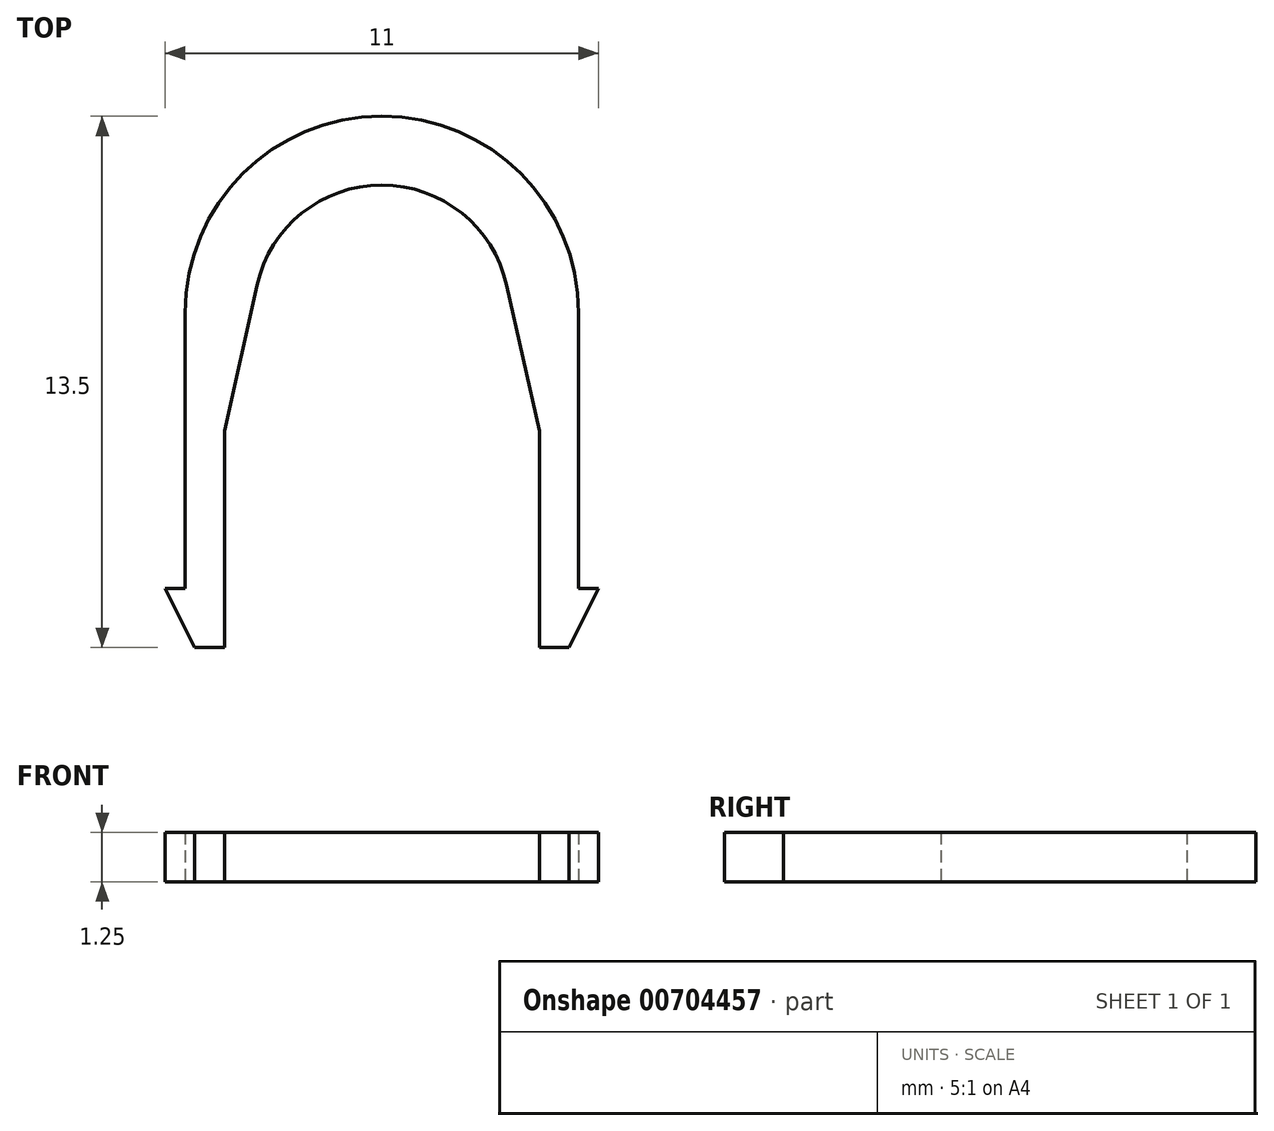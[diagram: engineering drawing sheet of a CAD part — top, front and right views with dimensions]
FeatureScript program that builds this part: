
annotation { "Feature Type Name" : "Feature", "Feature Type Description" : "" }
export const myFeature = defineFeature(function(context is Context, id is Id, definition is map)
    precondition{}
    {
        {
            var Q0;
            Q0=qCreatedBy(makeId("Top.planeOp"),FACE);
            var sketch = newSketch(context, id + "F0", { "sketchPlane" : qUnion([Q0])});
            skLineSegment(sketch, "E0", {"start": v(0, 0) * mm, "end": v(0, 5) * mm, "construction": true});
            skArc(sketch, "E1", {"start": v(5, 5) * mm, "mid": v(0, 10) * mm, "end": v(-5, 5) * mm});
            skLineSegment(sketch, "E2", {"start": v(-5, 5) * mm, "end": v(-5, -2) * mm});
            skLineSegment(sketch, "E3", {"start": v(-4, 2) * mm, "end": v(-4, -3.5) * mm});
            skLineSegment(sketch, "E4", {"start": v(-5, -2) * mm, "end": v(-5.5, -2) * mm});
            skLineSegment(sketch, "E5", {"start": v(-5.5, -2) * mm, "end": v(-4.75, -3.5) * mm});
            skLineSegment(sketch, "E6", {"start": v(-4, -3.5) * mm, "end": v(-4.75, -3.5) * mm});
            skLineSegment(sketch, "E7.MirrorCS", {"start": v(5, 5) * mm, "end": v(5, -2) * mm});
            skLineSegment(sketch, "E8.MirrorCS", {"start": v(5, -2) * mm, "end": v(5.5, -2) * mm});
            skLineSegment(sketch, "E9.MirrorCS", {"start": v(5.5, -2) * mm, "end": v(4.75, -3.5) * mm});
            skLineSegment(sketch, "E10.MirrorCS", {"start": v(4, -3.5) * mm, "end": v(4.75, -3.5) * mm});
            skLineSegment(sketch, "E11.MirrorCS", {"start": v(4, 2) * mm, "end": v(4, -3.5) * mm});
            skArc(sketch, "E12", {"start": v(3.17, 5.7) * mm, "mid": v(0, 8.25) * mm, "end": v(-3.17, 5.7) * mm});
            skLineSegment(sketch, "E13", {"start": v(-4, 2) * mm, "end": v(-3.17, 5.7) * mm});
            skLineSegment(sketch, "E14.MirrorCS", {"start": v(4, 2) * mm, "end": v(3.17, 5.7) * mm});
            skSolve(sketch);
        }
        {
            var Q0;
            Q0=makeQuery(id+"F0.imprint","IMPRINT",FACE,{"disambiguationData":[TD([[makeQuery(id+"F0.imprint","IMPRINT",EDGE,{"derivedFrom":sQuery(id+"F0.wireOp",EDGE,"E1")}),1.0]])]});
            extrude(context, id + "F1", {"entities" : qUnion([Q0]), "depth" : 1.25 * mm, "offsetDistance" : 25 * mm});
        }
    });
